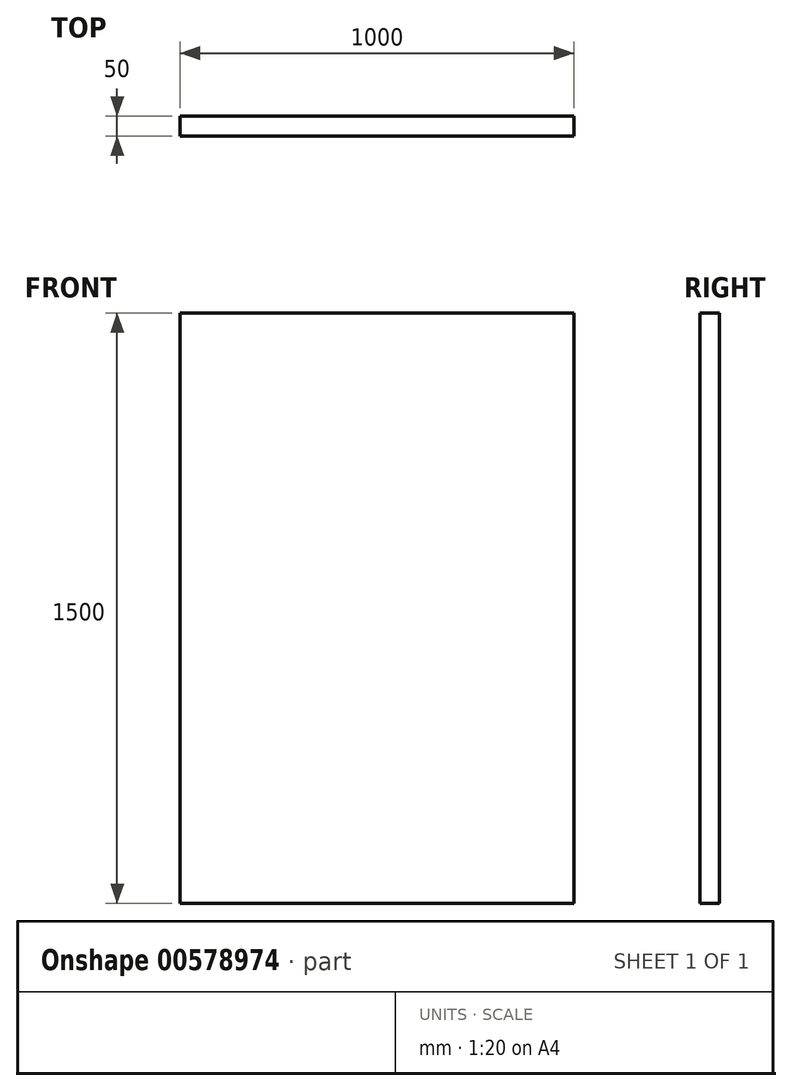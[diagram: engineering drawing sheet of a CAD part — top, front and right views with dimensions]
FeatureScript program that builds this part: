
annotation { "Feature Type Name" : "Feature", "Feature Type Description" : "" }
export const myFeature = defineFeature(function(context is Context, id is Id, definition is map)
    precondition{}
    {
        {
            var Q0;
            Q0=qCreatedBy(makeId("Front.planeOp"),FACE);
            var sketch = newSketch(context, id + "F0", { "sketchPlane" : qUnion([Q0])});
            skLineSegment(sketch, "E0.bottom", {"start": v(500, 750) * mm, "end": v(-500, 750) * mm});
            skLineSegment(sketch, "E0.top", {"start": v(500, -750) * mm, "end": v(-500, -750) * mm});
            skLineSegment(sketch, "E0.left", {"start": v(500, 750) * mm, "end": v(500, -750) * mm});
            skLineSegment(sketch, "E0.right", {"start": v(-500, 750) * mm, "end": v(-500, -750) * mm});
            skPoint(sketch, "E0.middle", {"position": v(0, 0) * mm});
            skSolve(sketch);
        }
        {
            var Q0;
            Q0=makeQuery(id+"F0.imprint","IMPRINT",FACE,{"disambiguationData":[TD([[makeQuery(id+"F0.imprint","IMPRINT",EDGE,{"derivedFrom":sQuery(id+"F0.wireOp",EDGE,"E0.bottom")}),1.0]])]});
            extrude(context, id + "F1", {"entities" : qUnion([Q0]), "endBound" : BoundingType.SYMMETRIC, "depth" : 50 * mm, "offsetDistance" : 25 * mm});
        }
    });
